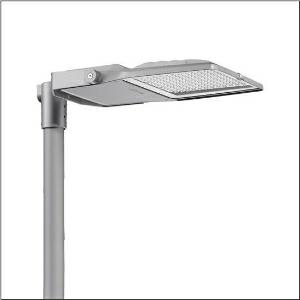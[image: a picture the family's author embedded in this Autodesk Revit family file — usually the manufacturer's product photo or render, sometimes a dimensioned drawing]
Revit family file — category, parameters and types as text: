
# Revit family: floodlight_fl_21_midi___pl64_5xa7786e2e3a_c0a1
name_source: partatom
category: Lighting Fixtures
units: mm (PartAtom-declared; Revit-internal decimal feet)

## family parameters
Cut with Voids When Loaded = No
Host = Face
Light Source = No
Part Type = Normal
Room Calculation Point = No
Round Connector Dimension = Use Diameter
Shared = No

## types (1)
- --- (1 x LED, 26020 lm, 212.4 W, 3000K)
    Apparent Load = 212 VA
    CIE Flux Codes = 28 80 98 100 100
    Color Rendering = 70
    Color Temperature = 3000K
    Default Elevation = 1800 mm
    Description = Floodlight FL 21 midi, floodlight, primary light control with lens, of PMMA, primary optical cover: protective disc, of toughened safety glass, transparent, light distribution: PL64, light emission: direct distribution, installation type: surface-mounted, LED, High Power LED, rated luminous flux: 26.020lm, luminous efficacy: 123lm/W, light colour: 730, colour temperature: 3000K, control gear: Smart Interface (Zhaga), control: flexible luminous flux parameterisation, time-dependent luminous flux control, constant luminous flux control, overheat protection, pre-setting: logarithmic dimming characteristic, with terminal, 6-pole, mains connection: 220..240V, AC, 50/60Hz, start of lifetime: 212W, end of service life: 231W, reduction: 95W, luminaire housing, of diecast aluminium, powder-coated, Siteco® metallic grey (DB 702S), corrosivity category C5 mid according to DIN EN ISO 12944, suitable for swimming pools, chlorine-resistant, sealing non-destructively replaceable, please order mast flange separately, mast bracket, of steel, galvanised, powder-coated, Siteco® metallic grey (DB 702S), Smart Interface below and above, protection rating (complete): IP66, insulation class (complete): insulation class II (safety insulation), certification: CE, ENEC, VDE, protection symbol: D, impact resistance: IK08, permissible operating ambient temperature: -40..+40°C, permissible operating ambient temperature for outdoor applications: -40..+50°C, standard: DIN EN 12944, LABS conformity tested according to VDMA 24364:2018-05, packaging unit: 1 piece

Light Distribution: PL64
    Height = 76 mm
    Lamp = 1 x LED
    Lamp Light Flux = 26020 lm
    Lamp Power = 212.4 W
    Lamp count = 1
    Length = 657 mm
    Luminous efficacy = 123 lm/W
    Manufacturer = Siteco
    ModVariant = No
    Model = 5XA7786E2E3A
    Number of Poles = 1
    OnlyDefault = Yes
    Power Factor = 1
    Product Name = Floodlight FL 21 midi | PL64
    Product group = floodlight | pylon annexe
    ProductGroupID = 6201
    Protection Class = Protection class II
    Protection Degree = IP 66
    RLX_Detail_Level = 1
    RLX_Emergency_Light_Flux = 0 lm
    RLX_Emergency_Type = 0
    RLX_Emergency_Type_DB = No
    RlxData = <blob elided: 153697 chars, md5=f8adec41>
    Socket = socket
    Standby Power = 0 W
    System Light Flux = 26020 lm
    System Power = 212 W
    Type Comments = factory setting: luminous flux: 100 % | dim-lin: 254 | 710 mA
    Type Image = l_1007123.jpg
    URL = http://relux.com
    VarID = @adj_201745
    Voltage = 0 V
    Weight = 0.00 kg
    Width = 442 mm

## geometry (parser evidence)
native form markers: Blend x4, Sweep x13
no freeform markers — native parametric forms only
